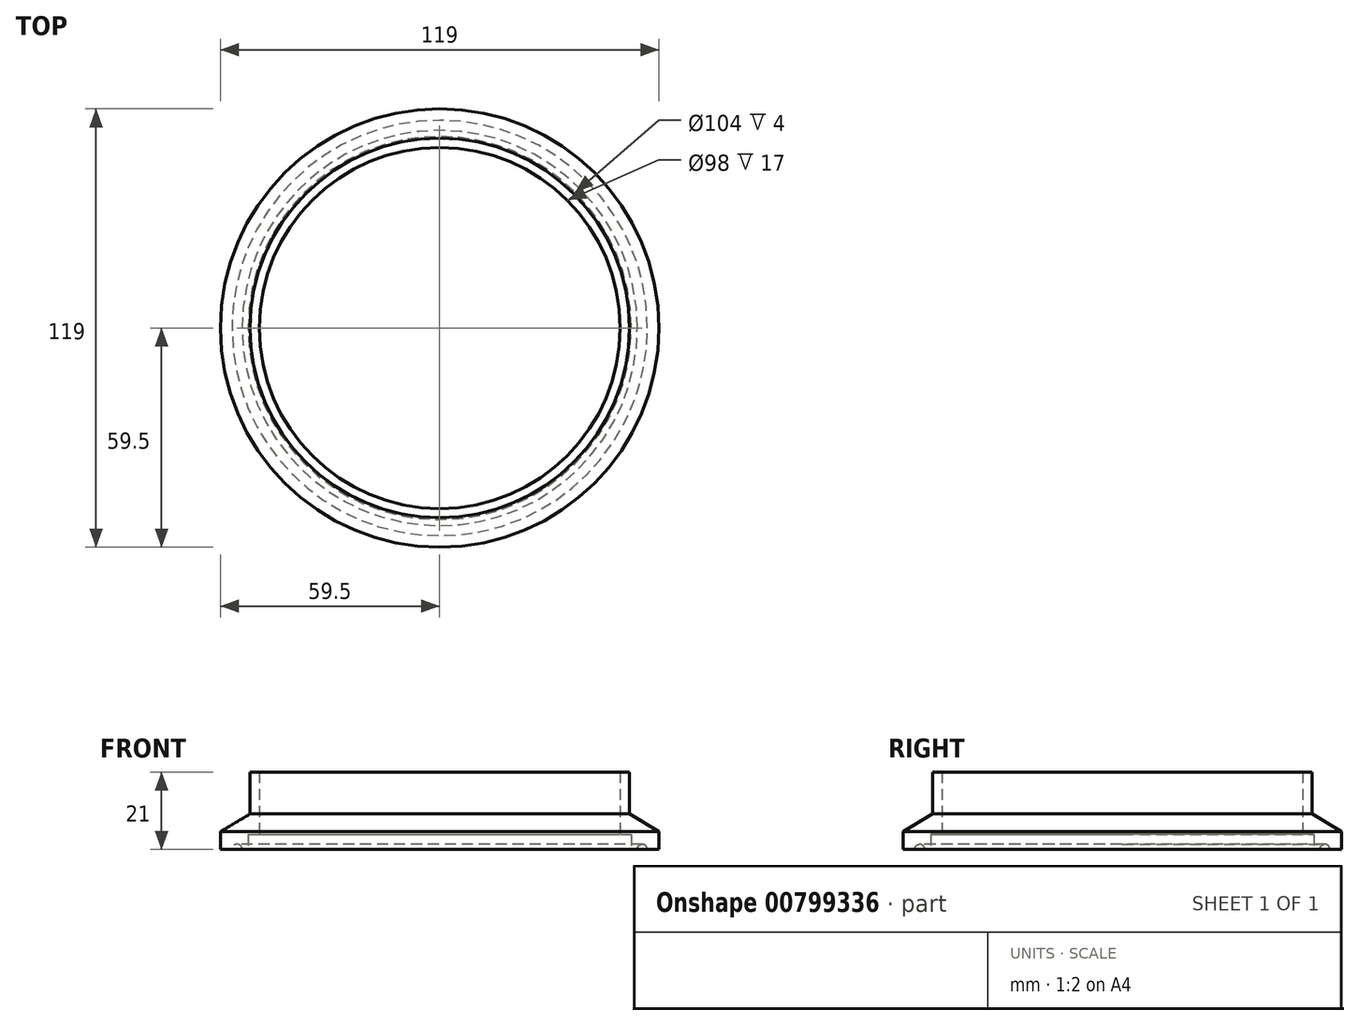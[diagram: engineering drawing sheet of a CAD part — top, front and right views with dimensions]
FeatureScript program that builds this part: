
annotation { "Feature Type Name" : "Feature", "Feature Type Description" : "" }
export const myFeature = defineFeature(function(context is Context, id is Id, definition is map)
    precondition{}
    {
        {
            var Q0;
            Q0=qCreatedBy(makeId("Front.planeOp"),FACE);
            var sketch = newSketch(context, id + "F0", { "sketchPlane" : qUnion([Q0])});
            skLineSegment(sketch, "E0", {"start": v(-51.5, -1.8) * mm, "end": v(-53.63, -1.8) * mm});
            skLineSegment(sketch, "E1", {"start": v(-51.5, 7.8) * mm, "end": v(-51.5, 19.2) * mm});
            skLineSegment(sketch, "E2", {"start": v(-51.5, 19.2) * mm, "end": v(-49, 19.2) * mm});
            skLineSegment(sketch, "E3", {"start": v(-49, 19.2) * mm, "end": v(-49, 2.2) * mm});
            skLineSegment(sketch, "E4", {"start": v(-59.5, -1.8) * mm, "end": v(-59.5, 3) * mm});
            skPoint(sketch, "E4.endSnap0", {"position": v(-51.5, 3) * mm});
            skLineSegment(sketch, "E5", {"start": v(-51.5, 7.8) * mm, "end": v(-59.5, 3) * mm});
            skArc(sketch, "E6", {"start": v(-53.63, -1.8) * mm, "mid": v(-55, -0.43) * mm, "end": v(-56.37, -1.8) * mm});
            skLineSegment(sketch, "E7.trimOffspring", {"start": v(-56.37, -1.8) * mm, "end": v(-59.5, -1.8) * mm});
            skLineSegment(sketch, "E8", {"start": v(0, 0) * mm, "end": v(0, 38.79) * mm, "construction": true});
            skLineSegment(sketch, "E9", {"start": v(0, -1.8) * mm, "end": v(-49, -1.8) * mm});
            skLineSegment(sketch, "E10", {"start": v(-52, -1.8) * mm, "end": v(-52, 2.2) * mm});
            skLineSegment(sketch, "E11", {"start": v(-52, 2.2) * mm, "end": v(-49, 2.2) * mm});
            skPoint(sketch, "E12.orphan", {"position": v(-49, -1.8) * mm});
            skLineSegment(sketch, "E13.trimOffspring", {"start": v(-51.5, -1.8) * mm, "end": v(-52, -1.8) * mm});
            skSolve(sketch);
        }
        {
            var Q0;
            Q0=qSketchRegion(id+"F0",true);
            var Q1;
            Q1=sQuery(id+"F0.wireOp",EDGE,"E8");
            revolve(context, id + "F1", {"entities" : qUnion([Q0]), "axis" : qUnion([Q1]), "revolveType" : RevolveType.FULL});
        }
    });
